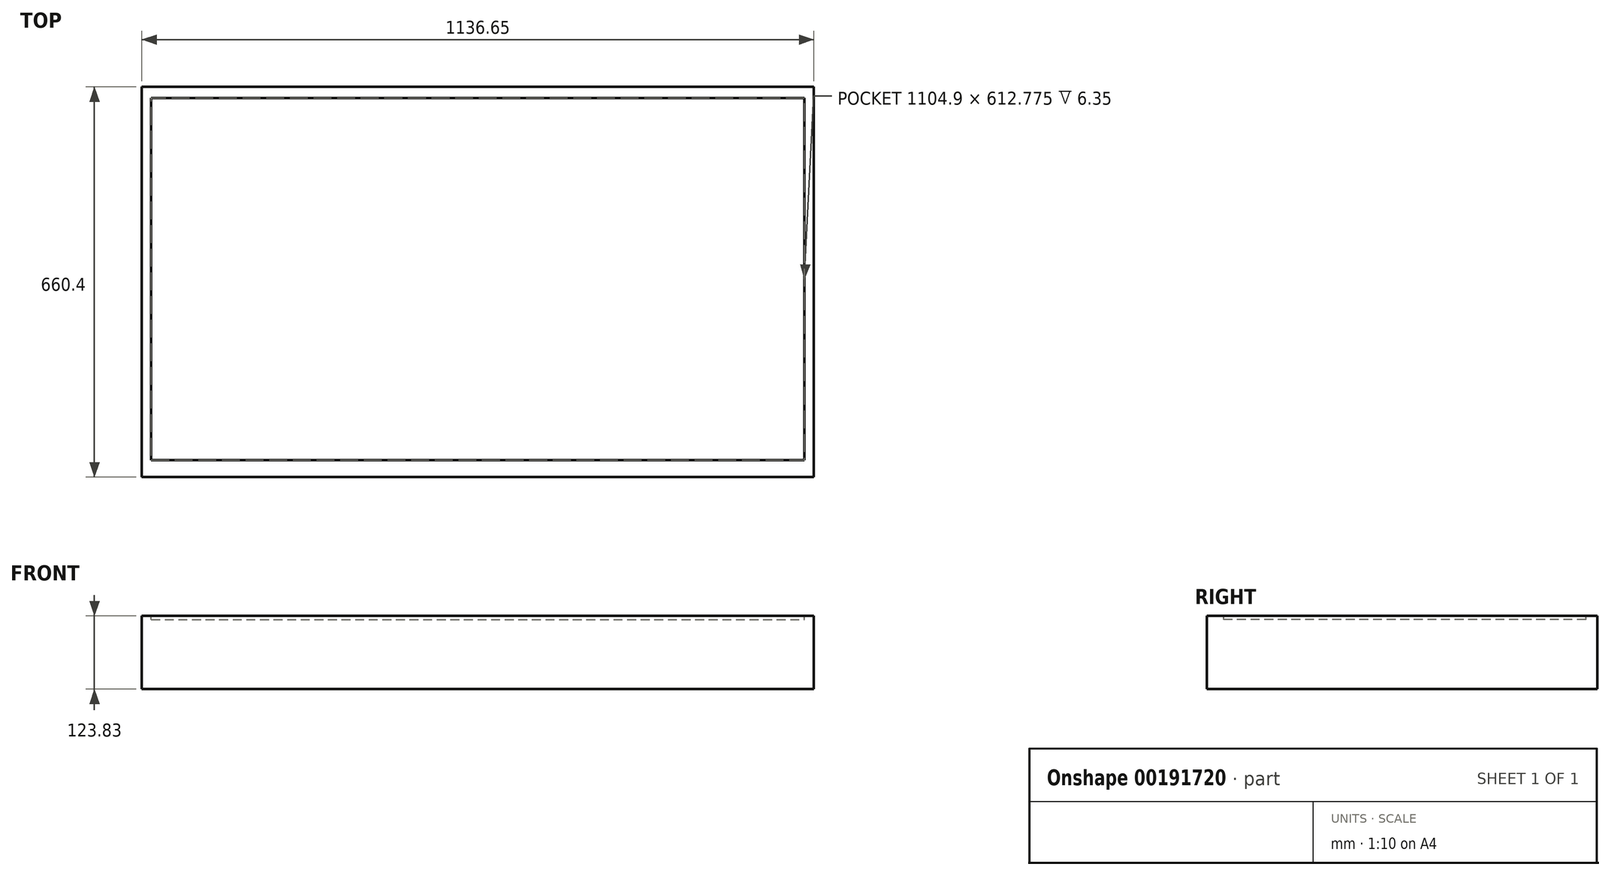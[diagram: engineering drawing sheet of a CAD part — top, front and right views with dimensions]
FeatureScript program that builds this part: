
annotation { "Feature Type Name" : "Feature", "Feature Type Description" : "" }
export const myFeature = defineFeature(function(context is Context, id is Id, definition is map)
    precondition{}
    {
        {
            var Q0;
            Q0=qCreatedBy(makeId("Top.planeOp"),FACE);
            var sketch = newSketch(context, id + "F0", { "sketchPlane" : qUnion([Q0])});
            skLineSegment(sketch, "E0.bottom", {"start": v(-596.65, 388.96) * mm, "end": v(540, 388.96) * mm});
            skLineSegment(sketch, "E0.top", {"start": v(-596.65, -271.44) * mm, "end": v(540, -271.44) * mm});
            skLineSegment(sketch, "E0.left", {"start": v(-596.65, 388.96) * mm, "end": v(-596.65, -271.44) * mm});
            skLineSegment(sketch, "E0.right", {"start": v(540, 388.96) * mm, "end": v(540, -271.44) * mm});
            skLineSegment(sketch, "E1.bottom", {"start": v(-580.78, 369.9) * mm, "end": v(524.12, 369.9) * mm});
            skLineSegment(sketch, "E1.top", {"start": v(-580.78, -242.87) * mm, "end": v(524.12, -242.87) * mm});
            skLineSegment(sketch, "E1.left", {"start": v(-580.78, 369.9) * mm, "end": v(-580.78, -242.87) * mm});
            skLineSegment(sketch, "E1.right", {"start": v(524.12, 369.9) * mm, "end": v(524.12, -242.87) * mm});
            skSolve(sketch);
        }
        {
            var Q0;
            Q0=makeQuery(id+"F0.imprint","IMPRINT",FACE,{"disambiguationData":[TD([[makeQuery(id+"F0.imprint","IMPRINT",EDGE,{"derivedFrom":sQuery(id+"F0.wireOp",EDGE,"E0.bottom")}),-1.0]])]});
            var Q1;
            Q1=makeQuery(id+"F0.imprint","IMPRINT",FACE,{"disambiguationData":[TD([[makeQuery(id+"F0.imprint","IMPRINT",EDGE,{"derivedFrom":sQuery(id+"F0.wireOp",EDGE,"E1.bottom")}),-1.0]])]});
            extrude(context, id + "F1", {"entities" : qUnion([Q0, Q1]), "oppositeDirection" : true, "depth" : 123.82 * mm});
        }
        {
            var Q0;
            Q0=makeQuery(id+"F0.imprint","IMPRINT",FACE,{"disambiguationData":[TD([[makeQuery(id+"F0.imprint","IMPRINT",EDGE,{"derivedFrom":sQuery(id+"F0.wireOp",EDGE,"E1.bottom")}),-1.0]])]});
            extrude(context, id + "F2", {"entities" : qUnion([Q0]), "operationType" : NewBodyOperationType.REMOVE, "oppositeDirection" : true, "depth" : 6.35 * mm});
        }
    });
